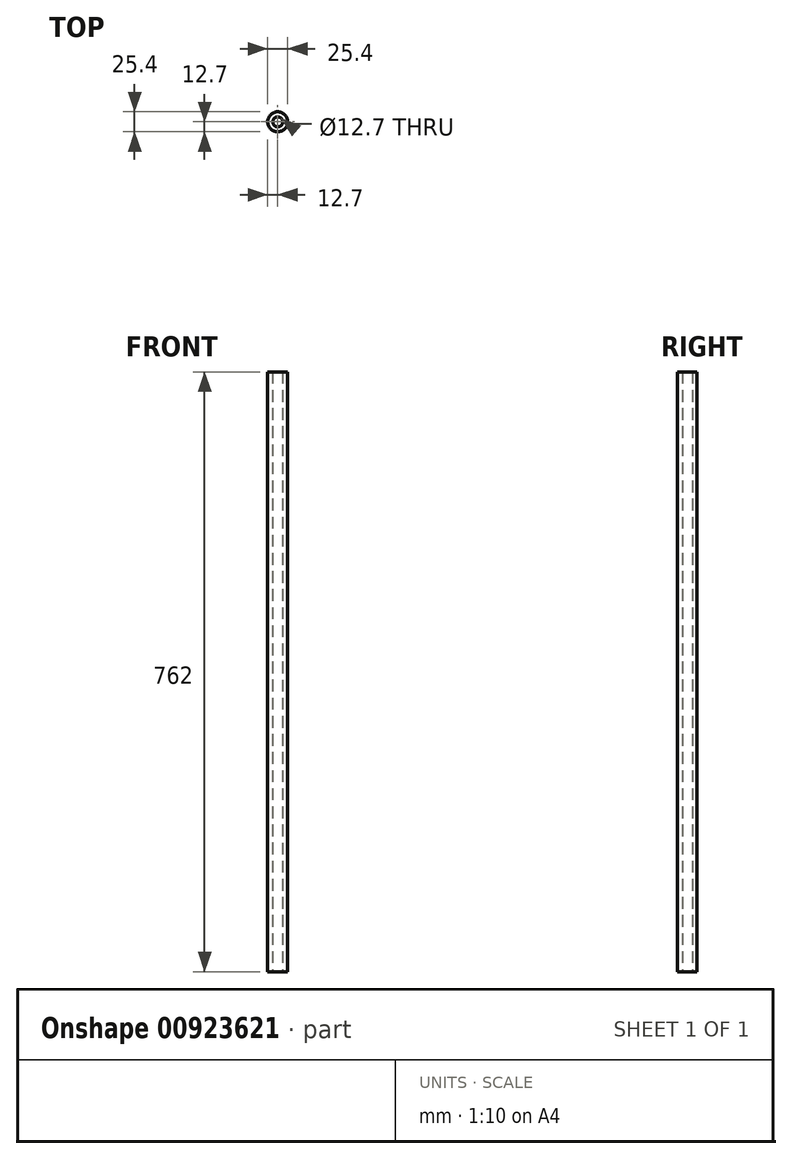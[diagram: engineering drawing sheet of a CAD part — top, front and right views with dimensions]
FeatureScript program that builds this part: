
annotation { "Feature Type Name" : "Feature", "Feature Type Description" : "" }
export const myFeature = defineFeature(function(context is Context, id is Id, definition is map)
    precondition{}
    {
        {
            var Q0;
            Q0=qCreatedBy(makeId("Top.planeOp"),FACE);
            var sketch = newSketch(context, id + "F0", { "sketchPlane" : qUnion([Q0])});
            skCircle(sketch, "E0", {"center": v(0, 0) * mm, "radius": 6.35 * mm});
            skCircle(sketch, "E1", {"center": v(0, 0) * mm, "radius": 12.7 * mm});
            skSolve(sketch);
        }
        {
            var Q0;
            Q0=qSketchRegion(id+"F0",true);
            extrude(context, id + "F1", {"entities" : qUnion([Q0]), "depth" : 762 * mm, "offsetDistance" : 25.4 * mm});
        }
    });
